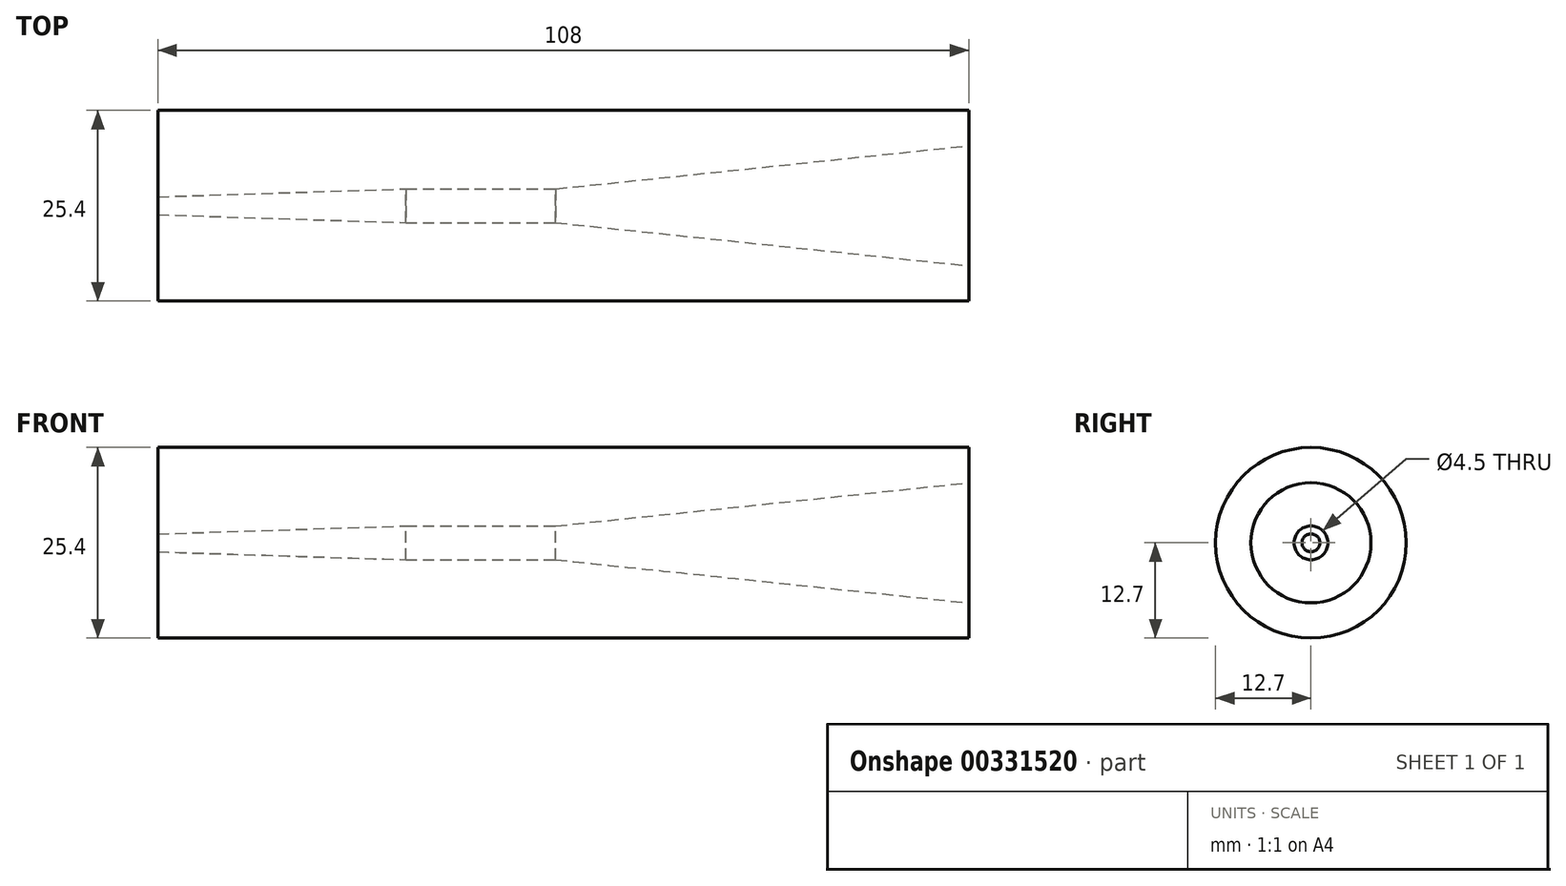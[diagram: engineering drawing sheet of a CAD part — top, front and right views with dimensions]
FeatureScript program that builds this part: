
annotation { "Feature Type Name" : "Feature", "Feature Type Description" : "" }
export const myFeature = defineFeature(function(context is Context, id is Id, definition is map)
    precondition{}
    {
        {
            var Q0;
            Q0=qCreatedBy(makeId("Right.planeOp"),FACE);
            var sketch = newSketch(context, id + "F0", { "sketchPlane" : qUnion([Q0])});
            skCircle(sketch, "E0", {"center": v(0, 0) * mm, "radius": 12.7 * mm});
            skSolve(sketch);
        }
        {
            var Q0;
            Q0=qCreatedBy(makeId("Front.planeOp"),FACE);
            var sketch = newSketch(context, id + "F1", { "sketchPlane" : qUnion([Q0])});
            skLineSegment(sketch, "E1", {"start": v(0, 0) * mm, "end": v(65, 0) * mm});
            skLineSegment(sketch, "E2", {"start": v(65, 0) * mm, "end": v(65, 8) * mm});
            skLineSegment(sketch, "E3", {"start": v(65, 8) * mm, "end": v(10, 2.25) * mm});
            skLineSegment(sketch, "E4", {"start": v(10, 2.25) * mm, "end": v(0, 2.25) * mm});
            skLineSegment(sketch, "E5", {"start": v(0, 2.25) * mm, "end": v(-10, 2.25) * mm});
            skLineSegment(sketch, "E6", {"start": v(-10, 2.25) * mm, "end": v(-43, 1.2) * mm});
            skLineSegment(sketch, "E7", {"start": v(-43, 1.2) * mm, "end": v(-43, 0) * mm});
            skLineSegment(sketch, "E8", {"start": v(-43, 0) * mm, "end": v(0, 0) * mm});
            skSolve(sketch);
        }
        {
            var Q0;
            Q0 = qSketchRegion(id + "F0", true);
            extrude(context, id + "F2", {"entities" : qUnion([Q0]), "depth" : 65 * mm, "hasSecondDirection" : true, "secondDirectionOppositeDirection" : true, "secondDirectionDepth" : 43 * mm});
        }
        {
            var Q0;
            Q0 = qSketchRegion(id + "F1", true);
            var Q1;
            Q1=sQuery(id+"F1.wireOp",EDGE,"E8");
            revolve(context, id + "F3", {"operationType" : NewBodyOperationType.REMOVE, "entities" : qUnion([Q0]), "axis" : qUnion([Q1]), "revolveType" : RevolveType.FULL, "oppositeDirection" : true});
        }
    });
